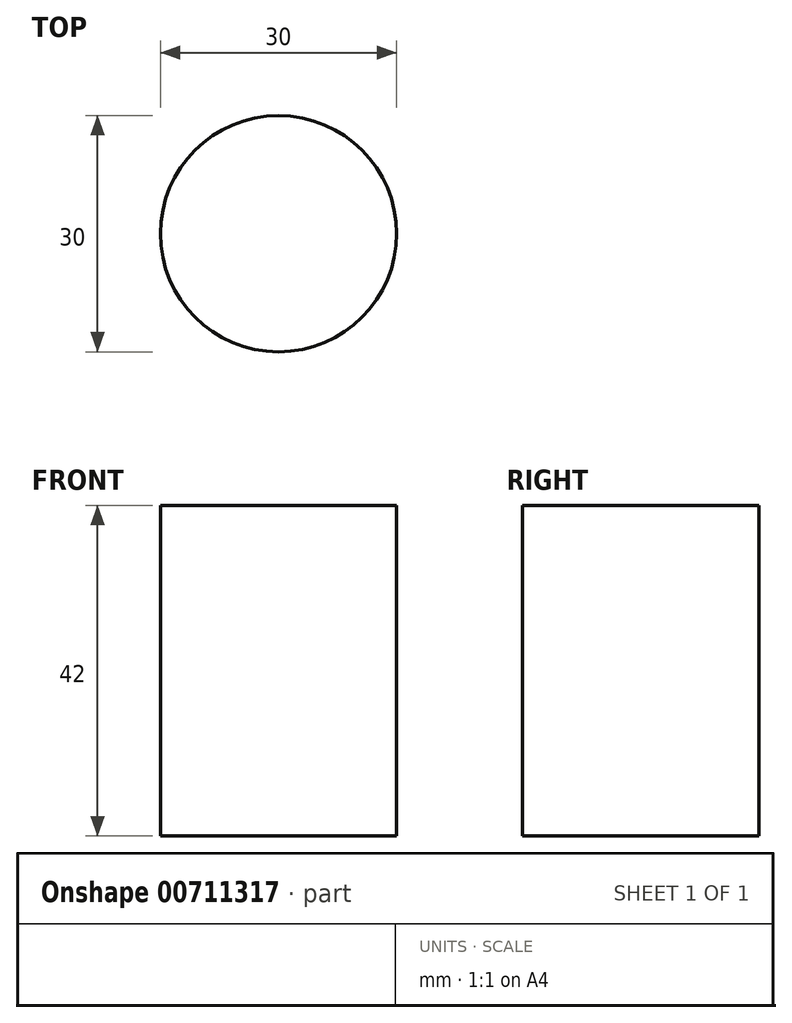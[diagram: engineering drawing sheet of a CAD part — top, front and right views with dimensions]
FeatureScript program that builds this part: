
annotation { "Feature Type Name" : "Feature", "Feature Type Description" : "" }
export const myFeature = defineFeature(function(context is Context, id is Id, definition is map)
    precondition{}
    {
        {
            var Q0;
            Q0=qCreatedBy(makeId("Top.planeOp"),FACE);
            var sketch = newSketch(context, id + "F0", { "sketchPlane" : qUnion([Q0])});
            skCircle(sketch, "E0", {"center": v(0, 0) * mm, "radius": 15 * mm});
            skSolve(sketch);
        }
        {
            var Q0;
            Q0=makeQuery(id+"F0.imprint","IMPRINT",FACE,{"disambiguationData":[TD([[makeQuery(id+"F0.imprint","IMPRINT",EDGE,{"derivedFrom":sQuery(id+"F0.wireOp",EDGE,"E0")}),1.0]])]});
            extrude(context, id + "F1", {"entities" : qUnion([Q0]), "depth" : 42 * mm, "offsetDistance" : 25 * mm});
        }
    });
